# Revit family: 303_R17_
name_source: partatom
category: Pipe Accessories
revit_build: Autodesk Revit 2018 (Build: 20170223_1515(x64)
units: mm (PartAtom-declared; Revit-internal decimal feet)

## family parameters
Always vertical = Yes
Cut with Voids When Loaded = No
Part Type = Valve - Breaks Into
Round Connector Dimension = Use Diameter
Shared = No
Work Plane-Based = No

## types (3) — shared parameters
CAT0 = Yes
Description = Straight lockshield valve for heat systems
L2D_Min = 3048 mm  [stored 10 ft]
L6 = 4 mm  [stored 0.0131234 ft]
L6__ve = -4 mm  [stored -0.0131234 ft]
L8 = 2 mm  [stored 0.00656168 ft]
L8__ve = -2 mm  [stored -0.00656168 ft]
LC = 52 mm  [stored 0.170604 ft]
Manufacturer = Giacomini
QmdConnectorList = 301;D;302;D1
URL = http://www.giacomini.com
Y2 = 8 mm  [stored 0.0262467 ft]
Y3 = 7 mm  [stored 0.0229659 ft]
magiPartTypeId = 303
magiProductFamilyId = R17*
zero-valued in all types: MC_Default_elevation

## per-type parameters (varying)
- R17X032: B4=5 mm  [stored 0.0164042 ft]; CenSd_K2_6=9 mm  [stored 0.0295276 ft]; CenSd_W2_6=12 mm  [stored 0.0393701 ft]; CenSd_YY_6=8 mm  [stored 0.0262467 ft]; D=10 mm; D1=10 mm; G3=10 mm  [stored 0.0328084 ft]; H1=9 mm  [stored 0.0295276 ft]; K2=11 mm; K3=8 mm  [stored 0.0262467 ft]; KCAT=Yes; KCAT1=No; L2=8 mm  [stored 0.0262467 ft]; L2D=54 mm; L4=6 mm  [stored 0.019685 ft]; L4__ve=-6 mm  [stored -0.019685 ft]; L5=8 mm  [stored 0.0262467 ft]; LC1=27 mm  [stored 0.0885827 ft]; LC2=45 mm  [stored 0.147638 ft]; LX=26 mm; R1=8 mm  [stored 0.0262467 ft]; W2=14 mm  [stored 0.0459318 ft]; W2D=10 mm  [stored 0.0328084 ft]; W4=8 mm  [stored 0.0262467 ft]; X11=12 mm  [stored 0.0393701 ft]; YY=10 mm  [stored 0.0328084 ft]
- R17X033: B4=6 mm  [stored 0.019685 ft]; CenSd_K2_6=11 mm; CenSd_W2_6=13 mm; CenSd_YY_6=10 mm  [stored 0.0328084 ft]; D=15 mm; D1=15 mm; G3=12 mm  [stored 0.0393701 ft]; H1=13 mm; K2=13 mm; K3=10 mm  [stored 0.0328084 ft]; KCAT=Yes; KCAT1=No; L2=9 mm  [stored 0.0295276 ft]; L2D=56 mm; L4=6 mm  [stored 0.019685 ft]; L4__ve=-6 mm  [stored -0.019685 ft]; L5=8 mm  [stored 0.0262467 ft]; LC1=28 mm; LC2=47 mm; LX=27 mm  [stored 0.0885827 ft]; R1=11 mm; W2=15 mm  [stored 0.0492126 ft]; W2D=15 mm  [stored 0.0492126 ft]; W4=9 mm  [stored 0.0295276 ft]; X11=13 mm; YY=11 mm
- R17EX037: B4=7 mm  [stored 0.0229659 ft]; CenSd_K2_6=11 mm; CenSd_W2_6=13 mm; CenSd_YY_6=10 mm  [stored 0.0328084 ft]; D=20 mm; D1=15 mm; G3=12 mm  [stored 0.0393701 ft]; H1=14 mm  [stored 0.0459318 ft]; K2=13 mm; K3=10 mm  [stored 0.0328084 ft]; KCAT=No; KCAT1=Yes; L2=9 mm  [stored 0.0295276 ft]; L2D=57 mm; L4=7 mm  [stored 0.0229659 ft]; L4__ve=-7 mm  [stored -0.0229659 ft]; L5=9 mm  [stored 0.0295276 ft]; LC1=29 mm; LC2=48 mm; LX=28 mm; R1=11 mm; W2=15 mm  [stored 0.0492126 ft]; W2D=15 mm  [stored 0.0492126 ft]; W4=9 mm  [stored 0.0295276 ft]; X11=13 mm; YY=11 mm

note: column(s) folded — value = type name in every type: magiProductCode, magiProductId

note: [stored X ft] marks values corroborated as IEEE doubles in the binary element streams (Revit-internal decimal feet)
